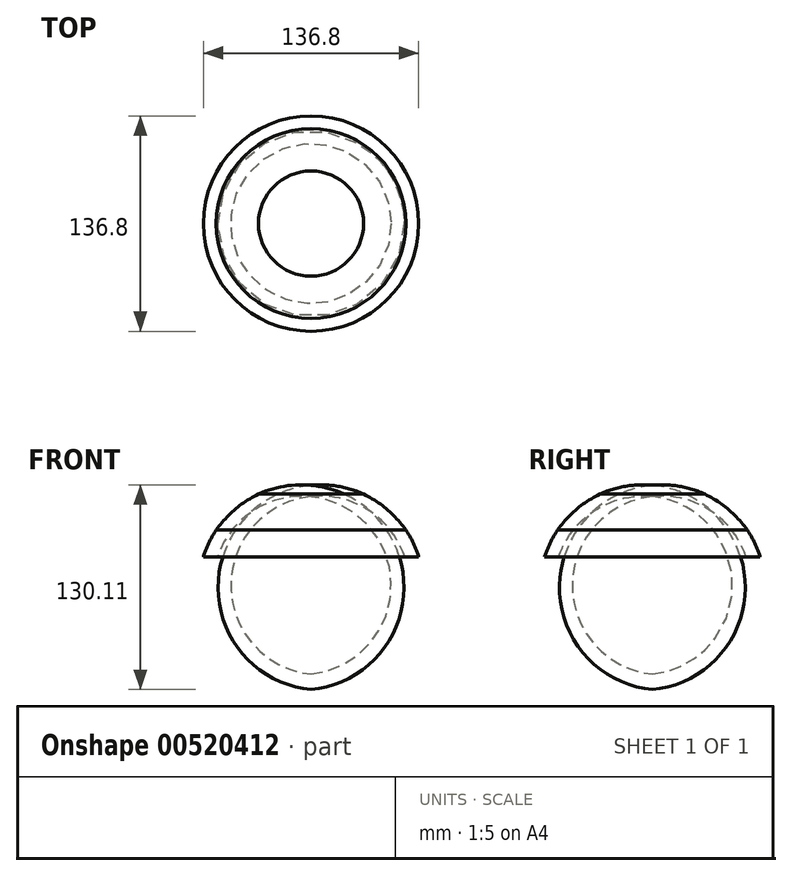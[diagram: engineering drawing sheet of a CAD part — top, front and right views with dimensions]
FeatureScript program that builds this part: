
annotation { "Feature Type Name" : "Feature", "Feature Type Description" : "" }
export const myFeature = defineFeature(function(context is Context, id is Id, definition is map)
    precondition{}
    {
        {
            var Q0;
            Q0=qCreatedBy(makeId("Front.planeOp"),FACE);
            var sketch = newSketch(context, id + "F0", { "sketchPlane" : qUnion([Q0])});
            skLineSegment(sketch, "E0", {"start": v(0, 0) * mm, "end": v(0, 79.7) * mm});
            skLineSegment(sketch, "E1", {"start": v(0, 79.7) * mm, "end": v(0, -83.25) * mm, "construction": true});
            skArc(sketch, "E2", {"start": v(68.4, 34.3) * mm, "mid": v(64.95, 43.03) * mm, "end": v(60.28, 51.19) * mm});
            skLineSegment(sketch, "E3", {"start": v(68.4, 34.3) * mm, "end": v(59.53, 34.3) * mm});
            skArc(sketch, "E4", {"start": v(59.53, 34.3) * mm, "mid": v(36.46, 63.83) * mm, "end": v(0, 72.53) * mm});
            skArc(sketch, "E5", {"start": v(60.28, 51.19) * mm, "mid": v(61, 79.28) * mm, "end": v(33.4, 74.04) * mm});
            skArc(sketch, "E6.trimOffspring", {"start": v(33.4, 74.04) * mm, "mid": v(17.08, 79.07) * mm, "end": v(0, 79.7) * mm});
            skArc(sketch, "E7", {"start": v(60.28, 51.19) * mm, "mid": v(53.56, 70.51) * mm, "end": v(33.4, 74.04) * mm});
            skArc(sketch, "E8", {"start": v(60.28, 51.19) * mm, "mid": v(48.28, 64.3) * mm, "end": v(33.4, 74.04) * mm});
            skPoint(sketch, "E9.start.orphan", {"position": v(17.08, 79.07) * mm});
            skSolve(sketch);
        }
        {
            var Q0;
            {var subQ0=sQuery(id+"F0.wireOp",EDGE,"E2");Q0=makeQuery(id+"F0.imprint","IMPRINT",FACE,{"disambiguationData":[TD([[makeQuery(id+"F0.imprint","IMPRINT",EDGE,{"derivedFrom":subQ0}),1.0]])]});}
            var Q1;
            Q1=sQuery(id+"F0.wireOp",EDGE,"E0");
            revolve(context, id + "F1", {"entities" : qUnion([Q0]), "axis" : qUnion([Q1]), "revolveType" : RevolveType.FULL});
        }
    });
